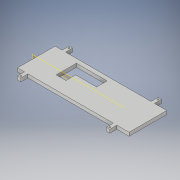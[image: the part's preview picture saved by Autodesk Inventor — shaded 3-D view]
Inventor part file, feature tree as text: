
AUTODESK INVENTOR PART (.ipt)
format: ipt  version: 2018 (Build 220112000, 112)  size: 156,160 bytes
history: native  units: in
note: dims shown in document units (in); Inventor stores cm internally (conversion verified against a paired STEP export)
features: extrude x3, sketch x3, plane x1, mirror x1
ambient origin geometry x8: Origin, YZ Plane, XZ Plane, XY Plane, X Axis, Y Axis, Z Axis, Center Point
bodies: Solid1 (feature_tree)
feature tree (8):
  extrude  "Extrusion1"  Depth=2.7in
  extrude  "Extrusion2"  TaperAngle=0.0deg  [1 undecoded]
  plane  "Work Plane1"
  mirror  "Mirror1"
  extrude  "Extrusion3"  Depth=0.5in
  sketch  "Sketch1"  dims[d0=8.0in d1=2.7in]
  sketch  "Sketch2"  dims[d2=0.25in d3=0.0in]
  sketch  "Sketch3"  dims[d4=0.5in d5=0.25in d6=0.11in d7=0.125in d8=0.125in d9=0.0in d10=0.5in d11=0.5in d12=0.25in d13=0.11in d14=0.125in d15=0.125in d16=0.0in d18=0.25in d19=0.0in d20=1.0in d21=0.75in d22=2.2in d23=0.7in d24=0.7in d25=0.3in d26=1.0in d27=0.0in d28=1.2in]
note: 1 required parameter value undecoded (feature->parameter linkage not recoverable at this tier; creation-order binding heuristic only, values carry confidence <= 0.55)
